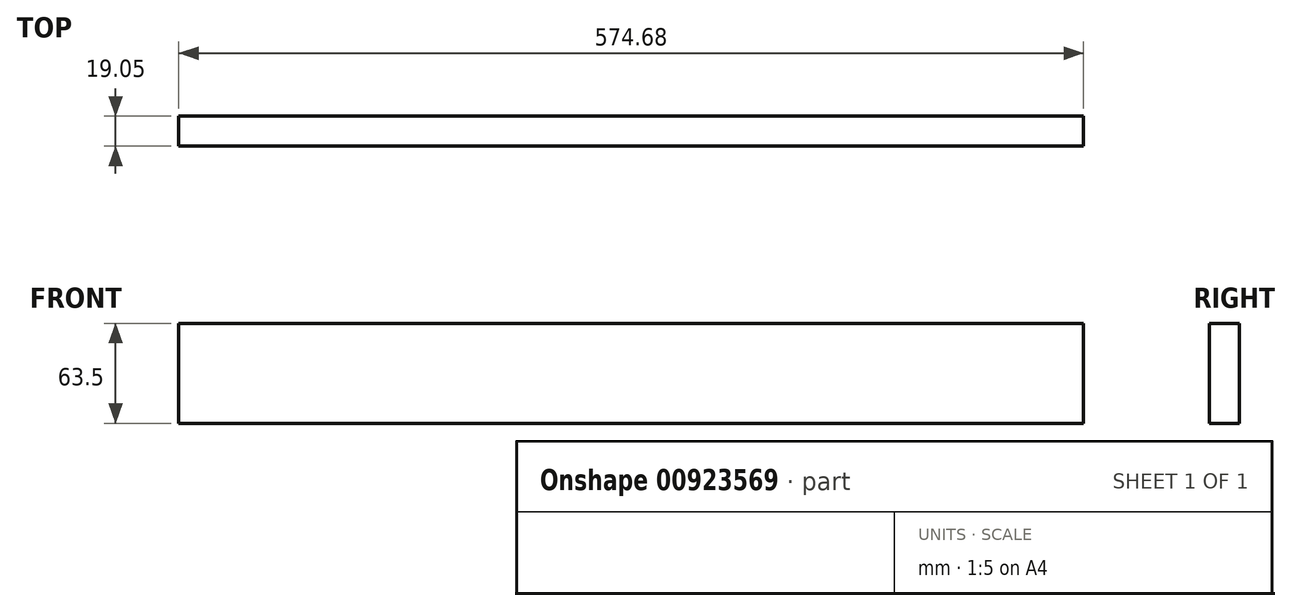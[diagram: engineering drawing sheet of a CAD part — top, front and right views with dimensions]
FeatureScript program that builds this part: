
annotation { "Feature Type Name" : "Feature", "Feature Type Description" : "" }
export const myFeature = defineFeature(function(context is Context, id is Id, definition is map)
    precondition{}
    {
        {
            var Q0;
            Q0=qCreatedBy(makeId("Front.planeOp"),FACE);
            var sketch = newSketch(context, id + "F0", { "sketchPlane" : qUnion([Q0])});
            skLineSegment(sketch, "E0.bottom", {"start": v(0, 0) * mm, "end": v(574.68, 0) * mm});
            skLineSegment(sketch, "E0.top", {"start": v(0, 63.5) * mm, "end": v(574.68, 63.5) * mm});
            skLineSegment(sketch, "E0.left", {"start": v(0, 0) * mm, "end": v(0, 63.5) * mm});
            skLineSegment(sketch, "E0.right", {"start": v(574.68, 0) * mm, "end": v(574.68, 63.5) * mm});
            skSolve(sketch);
        }
        {
            var Q0;
            Q0=makeQuery(id+"F0.imprint","IMPRINT",FACE,{"disambiguationData":[TD([[makeQuery(id+"F0.imprint","IMPRINT",EDGE,{"derivedFrom":sQuery(id+"F0.wireOp",EDGE,"E0.bottom")}),1.0]])]});
            extrude(context, id + "F1", {"entities" : qUnion([Q0]), "depth" : 19.05 * mm, "offsetDistance" : 25.4 * mm});
        }
    });
